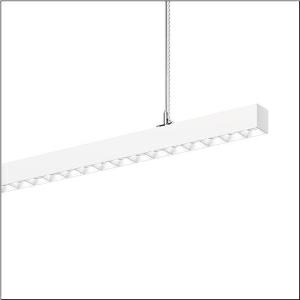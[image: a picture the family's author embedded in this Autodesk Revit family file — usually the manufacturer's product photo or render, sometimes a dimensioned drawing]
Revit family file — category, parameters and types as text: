
# Revit family: silica_r__21_51mx37da47wb_26de
name_source: partatom
category: Lighting Fixtures
units: mm (PartAtom-declared; Revit-internal decimal feet)

## family parameters
Cut with Voids When Loaded = No
Host = Face
Light Source = No
Part Type = Normal
Room Calculation Point = No
Round Connector Dimension = Use Diameter
Shared = No

## types (1)
- --- (1 x LED, 7300 lm, 44 W, 4000K)
    Apparent Load = 44 VA
    CIE Flux Codes = 71 92 99 59 100
    Color Rendering = 80
    Color Temperature = 4000K
    Default Elevation = 1800 mm
    Description = Silica® 21, office luminaire, primary light control with darklight reflector, of PMMA, white, CAT 2 (L<= 3000cd/m²), light emission: direct/indirect distribution, primary light characteristic: asymmetric, installation type: suspended mounting, LED, rated luminous flux: 7.300lm, luminous efficacy: 166lm/W, light colour: 840, colour temperature: 4000K, with terminal, 3+2-pole, max. 2.5mm², mains connection: 220..240V, AC, 50/60Hz, rated input power: 44W, luminaire housing, of aluminium, traffic white (RAL 9016), length: 1.204mm, width: 53mm, height: 53mm, protection rating (complete): IP20, insulation class (complete): insulation class I (protective earthing), certification: CE, permissible operating ambient temperature: 0..+35°C, standard: EN 50419, packaging unit: 1 piece
    Height = 53 mm
    Lamp = 1 x LED
    Lamp Light Flux = 7300 lm
    Lamp Power = 44 W
    Lamp count = 1
    Length = 1204 mm
    Luminous efficacy = 166 lm/W
    Manufacturer = Siteco
    ModVariant = No
    Model = 51MX37DA47WB
    Mounting Place = Ceiling
    Mounting Type = Pendant
    Number of Poles = 1
    OnlyDefault = Yes
    Power Factor = 1
    Product Name = Silica® 21
    Product group = office luminaire | ceiling pendant
    ProductGroupID = 902
    Protection Class = Protection class I
    Protection Degree = IP 20
    RLX_Detail_Level = 1
    RLX_Emergency_Light_Flux = 0 lm
    RLX_Emergency_Type = 0
    RLX_Emergency_Type_DB = No
    RlxData = <blob elided: 42237 chars, md5=e0cb75a1>
    Socket = socket
    Standby Power = 0 W
    System Light Flux = 7300 lm
    System Power = 44 W
    Type Comments = factory setting: luminous flux: 100 % | dim-lin: 254 | 368 mA
    Type Image = l_1297797.jpg
    URL = http://relux.com
    VarID = @adj_050369
    Voltage = 0 V
    Weight = 0.00 kg
    Width = 53 mm

## geometry (parser evidence)
native form markers: Blend x4, Sweep x13
no freeform markers — native parametric forms only
